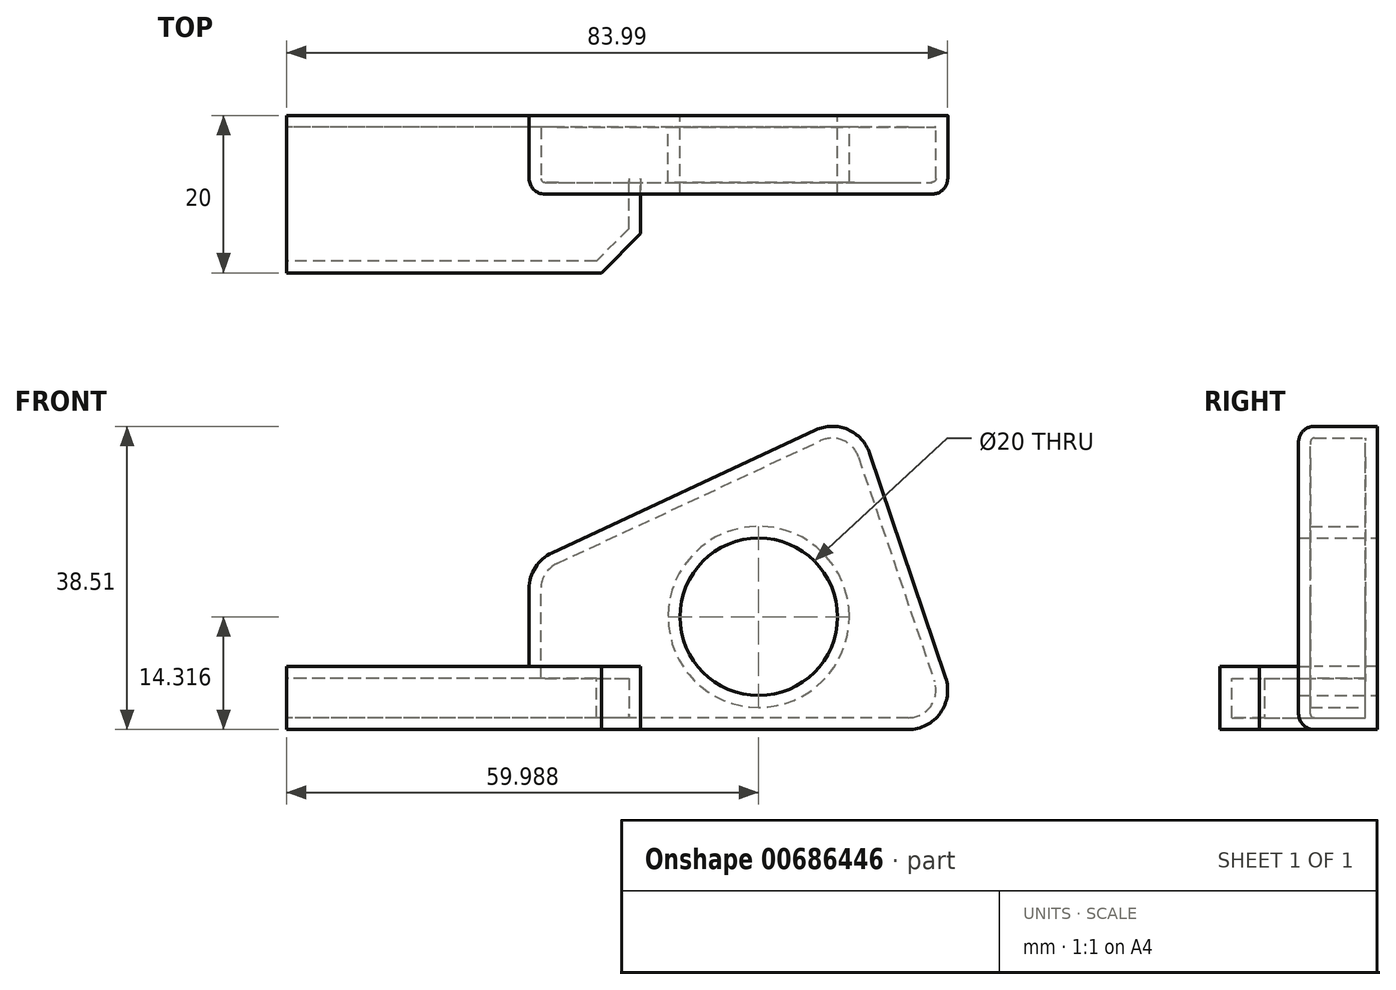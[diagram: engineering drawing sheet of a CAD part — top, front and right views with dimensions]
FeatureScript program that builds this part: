
annotation { "Feature Type Name" : "Feature", "Feature Type Description" : "" }
export const myFeature = defineFeature(function(context is Context, id is Id, definition is map)
    precondition{}
    {
        {
            var Q0;
            Q0=qCreatedBy(makeId("Front.planeOp"),FACE);
            var sketch = newSketch(context, id + "F0", { "sketchPlane" : qUnion([Q0])});
            skLineSegment(sketch, "E0", {"start": v(-17.15, 5) * mm, "end": v(-17.15, 17.9) * mm});
            skLineSegment(sketch, "E1", {"start": v(-14.26, 22.43) * mm, "end": v(19.25, 38.04) * mm});
            skLineSegment(sketch, "E2", {"start": v(26.1, 35.12) * mm, "end": v(35.75, 6.6) * mm});
            skLineSegment(sketch, "E3", {"start": v(31.01, 0) * mm, "end": v(-12.15, 0) * mm});
            skPoint(sketch, "E4.orphan", {"position": v(37.99, 0) * mm});
            skArc(sketch, "E5.filletArc", {"start": v(31.01, 0) * mm, "mid": v(35.08, 2.09) * mm, "end": v(35.75, 6.6) * mm});
            skPoint(sketch, "E6.visualSharp", {"position": v(-17.15, 21.09) * mm});
            skArc(sketch, "E6.filletArc", {"start": v(-14.26, 22.43) * mm, "mid": v(-16.37, 20.59) * mm, "end": v(-17.15, 17.9) * mm});
            skPoint(sketch, "E7.visualSharp", {"position": v(24.3, 40.4) * mm});
            skArc(sketch, "E7.filletArc", {"start": v(26.1, 35.12) * mm, "mid": v(23.32, 38.1) * mm, "end": v(19.25, 38.04) * mm});
            skPoint(sketch, "E8.visualSharp", {"position": v(-17.15, 0) * mm});
            skArc(sketch, "E8.filletArc", {"start": v(-17.15, 5) * mm, "mid": v(-15.69, 1.46) * mm, "end": v(-12.15, 0) * mm});
            skCircle(sketch, "E9", {"center": v(12, 14.32) * mm, "radius": 10 * mm});
            skSolve(sketch);
        }
        {
            var Q0;
            Q0=makeQuery(id+"F0.imprint","IMPRINT",FACE,{"disambiguationData":[TD([[makeQuery(id+"F0.imprint","IMPRINT",EDGE,{"derivedFrom":sQuery(id+"F0.wireOp",EDGE,"E0")}),-1.0]])]});
            extrude(context, id + "F1", {"entities" : qUnion([Q0]), "depth" : 10 * mm, "offsetDistance" : 25 * mm});
        }
        {
            var Q0;
            Q0=qCreatedBy(makeId("Front.planeOp"),FACE);
            var sketch = newSketch(context, id + "F2", { "sketchPlane" : qUnion([Q0])});
            skLineSegment(sketch, "E10.bottom", {"start": v(-2.98, 0) * mm, "end": v(-47.98, 0) * mm});
            skLineSegment(sketch, "E10.top", {"start": v(-2.98, 8) * mm, "end": v(-47.98, 8) * mm});
            skLineSegment(sketch, "E10.left", {"start": v(-2.98, 0) * mm, "end": v(-2.98, 8) * mm});
            skLineSegment(sketch, "E10.right", {"start": v(-47.98, 0) * mm, "end": v(-47.98, 8) * mm});
            skLineSegment(sketch, "E11", {"start": v(-2.98, -4.2) * mm, "end": v(-2.98, -41.4) * mm});
            skSolve(sketch);
        }
        {
            var Q0;
            Q0=makeQuery(id+"F2.imprint","IMPRINT",FACE,{"disambiguationData":[TD([[makeQuery(id+"F2.imprint","IMPRINT",EDGE,{"derivedFrom":sQuery(id+"F2.wireOp",EDGE,"E10.bottom")}),-1.0]])]});
            extrude(context, id + "F3", {"entities" : qUnion([Q0]), "operationType" : NewBodyOperationType.ADD, "depth" : 20 * mm, "offsetDistance" : 25 * mm});
        }
        {
            var Q0;
            Q0=makeQuery(id+"F3.opExtrude","CAP_EDGE",EDGE,{"disambiguationData":[OSD([sQuery(id+"F2.wireOp",EDGE,"E10.left")])],"isStart":false});
            chamfer(context, id + "F4", {"entities" : qUnion([Q0]), "width" : 5 * mm, "tangentPropagation" : true});
        }
        {
            var Q0;
            Q0=makeQuery(id+"F1.opExtrude","CAP_EDGE",EDGE,{"disambiguationData":[OSD([sQuery(id+"F0.wireOp",EDGE,"E0")])],"isStart":false});
            var Q1;
            Q1=makeQuery(id+"F1.opExtrude","CAP_EDGE",EDGE,{"disambiguationData":[OSD([sQuery(id+"F0.wireOp",EDGE,"E6.filletArc")])],"isStart":false});
            var Q2;
            Q2=makeQuery(id+"F1.opExtrude","CAP_EDGE",EDGE,{"disambiguationData":[OSD([sQuery(id+"F0.wireOp",EDGE,"E1")])],"isStart":false});
            var Q3;
            Q3=makeQuery(id+"F1.opExtrude","CAP_EDGE",EDGE,{"disambiguationData":[OSD([sQuery(id+"F0.wireOp",EDGE,"E7.filletArc")])],"isStart":false});
            var Q4;
            Q4=makeQuery(id+"F1.opExtrude","CAP_EDGE",EDGE,{"disambiguationData":[OSD([sQuery(id+"F0.wireOp",EDGE,"E2")])],"isStart":false});
            var Q5;
            Q5=makeQuery(id+"F1.opExtrude","CAP_EDGE",EDGE,{"disambiguationData":[OSD([sQuery(id+"F0.wireOp",EDGE,"E5.filletArc")])],"isStart":false});
            var Q6;
            Q6=makeQuery(id+"F1.opExtrude","CAP_EDGE",EDGE,{"disambiguationData":[OSD([sQuery(id+"F0.wireOp",EDGE,"E3")])],"isStart":false});
            fillet(context, id + "F5", {"entities" : qUnion([Q0, Q1, Q2, Q3, Q4, Q5, Q6]), "radius" : 2 * mm, "tangentPropagation" : true, "allowEdgeOverflow" : false});
        }
        {
            var Q0;
            Q0=makeQuery(id+"F3.opExtrude","SWEPT_FACE",FACE,{"disambiguationData":[OSD([sQuery(id+"F2.wireOp",EDGE,"E10.right")])]});
            shell(context, id + "F6", {"entities" : qUnion([Q0]), "thickness" : 1.5 * mm});
        }
    });
